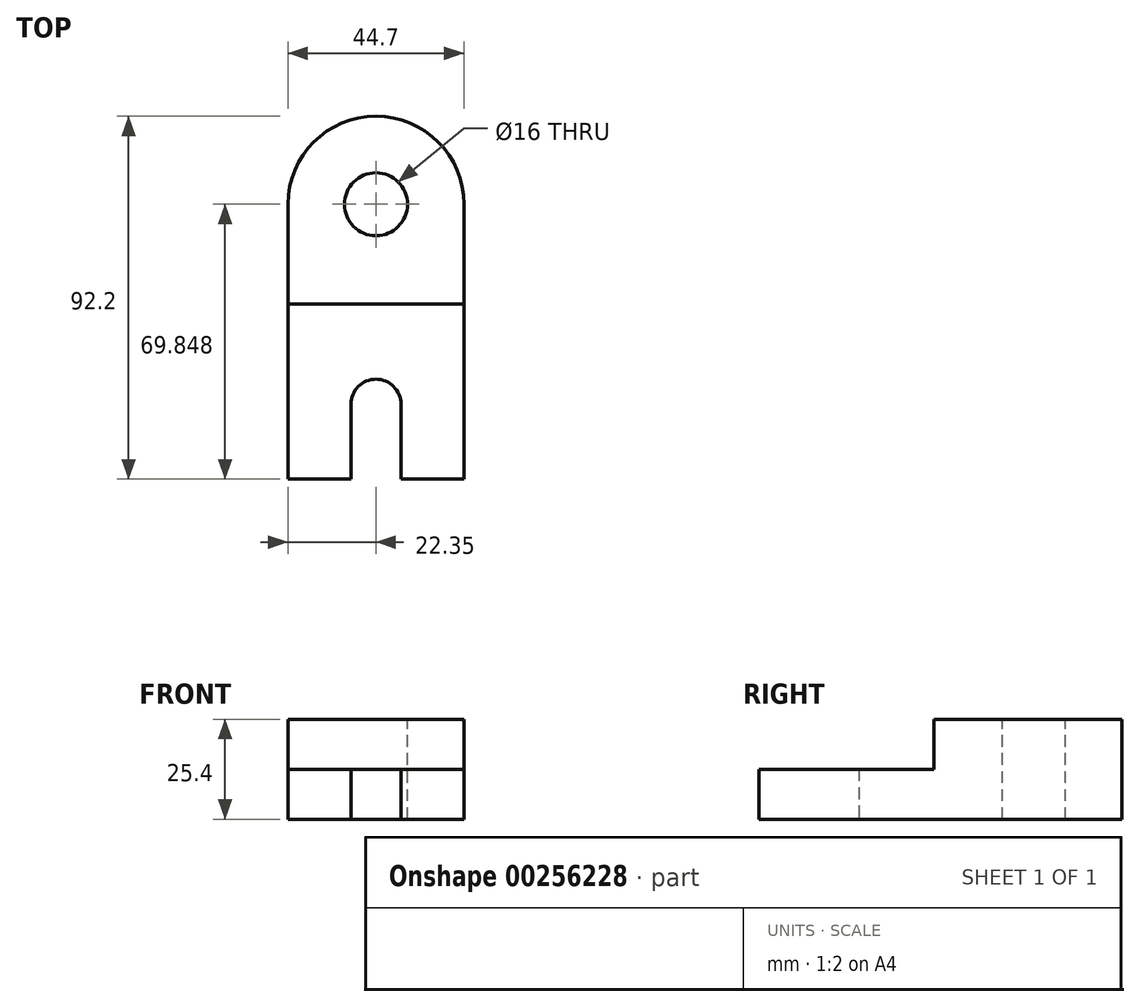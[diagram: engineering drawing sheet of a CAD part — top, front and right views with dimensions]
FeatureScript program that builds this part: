
annotation { "Feature Type Name" : "Feature", "Feature Type Description" : "" }
export const myFeature = defineFeature(function(context is Context, id is Id, definition is map)
    precondition{}
    {
        {
            var Q0;
            Q0=qCreatedBy(makeId("Top.planeOp"),FACE);
            var sketch = newSketch(context, id + "F0", { "sketchPlane" : qUnion([Q0])});
            skLineSegment(sketch, "E0", {"start": v(-5.13, 29.77) * mm, "end": v(-5.13, -40.08) * mm});
            skLineSegment(sketch, "E1", {"start": v(-49.83, 29.77) * mm, "end": v(-49.83, -40.08) * mm});
            skArc(sketch, "E2", {"start": v(-5.13, 29.77) * mm, "mid": v(-27.48, 52.12) * mm, "end": v(-49.83, 29.77) * mm});
            skLineSegment(sketch, "E3", {"start": v(-49.83, -40.08) * mm, "end": v(-33.83, -40.08) * mm});
            skLineSegment(sketch, "E4", {"start": v(-5.13, -40.08) * mm, "end": v(-21.13, -40.08) * mm});
            skLineSegment(sketch, "E5", {"start": v(-21.13, -40.08) * mm, "end": v(-21.13, -21.03) * mm});
            skLineSegment(sketch, "E6", {"start": v(-33.83, -40.08) * mm, "end": v(-33.83, -21.03) * mm});
            skArc(sketch, "E7", {"start": v(-21.13, -21.03) * mm, "mid": v(-27.48, -14.68) * mm, "end": v(-33.83, -21.03) * mm});
            skSolve(sketch);
        }
        {
            var Q0;
            Q0=makeQuery(id+"F0.imprint","IMPRINT",FACE,{"disambiguationData":[TD([[makeQuery(id+"F0.imprint","IMPRINT",EDGE,{"derivedFrom":sQuery(id+"F0.wireOp",EDGE,"E0")}),-1.0]])]});
            extrude(context, id + "F1", {"entities" : qUnion([Q0]), "depth" : 12.7 * mm});
        }
        {
            var Q0;
            Q0=makeQuery(id+"F1.opExtrude","CAP_FACE",FACE,{"disambiguationData":[OSD([sQuery(id+"F0.wireOp",EDGE,"E0"),sQuery(id+"F0.wireOp",EDGE,"E1"),sQuery(id+"F0.wireOp",EDGE,"E2"),sQuery(id+"F0.wireOp",EDGE,"E3"),sQuery(id+"F0.wireOp",EDGE,"E4"),sQuery(id+"F0.wireOp",EDGE,"E5"),sQuery(id+"F0.wireOp",EDGE,"E6"),sQuery(id+"F0.wireOp",EDGE,"E7")])],"isStart":false});
            var sketch = newSketch(context, id + "F2", { "sketchPlane" : qUnion([Q0])});
            skLineSegment(sketch, "E8", {"start": v(-49.83, 4.37) * mm, "end": v(-5.13, 4.37) * mm});
            skLineSegment(sketch, "E9", {"start": v(-49.83, 4.37) * mm, "end": v(-49.83, 29.77) * mm});
            skLineSegment(sketch, "E10", {"start": v(-5.13, 4.37) * mm, "end": v(-5.13, 29.77) * mm});
            skArc(sketch, "E11", {"start": v(-5.13, 29.77) * mm, "mid": v(-27.48, 52.12) * mm, "end": v(-49.83, 29.77) * mm});
            skSolve(sketch);
        }
        {
            var Q0;
            Q0=makeQuery(id+"F2.imprint","IMPRINT",FACE,{"disambiguationData":[TD([[makeQuery(id+"F2.imprint","IMPRINT",EDGE,{"derivedFrom":sQuery(id+"F2.wireOp",EDGE,"E8")}),1.0]])]});
            extrude(context, id + "F3", {"entities" : qUnion([Q0]), "operationType" : NewBodyOperationType.ADD, "depth" : 12.7 * mm});
        }
        {
            var Q0;
            Q0=makeQuery(id+"F3.opExtrude","CAP_FACE",FACE,{"disambiguationData":[OSD([sQuery(id+"F2.wireOp",EDGE,"E8"),sQuery(id+"F2.wireOp",EDGE,"E9"),sQuery(id+"F2.wireOp",EDGE,"E10"),sQuery(id+"F2.wireOp",EDGE,"E11")])],"isStart":false});
            var sketch = newSketch(context, id + "F4", { "sketchPlane" : qUnion([Q0])});
            skCircle(sketch, "E12", {"center": v(-27.48, 29.77) * mm, "radius": 8 * mm});
            skSolve(sketch);
        }
        {
            var Q0;
            Q0=sQuery(id+"F4.wireOp",VERTEX,"E12.center");
            var Q1;
            Q1=makeQuery(id+"F1.opExtrude","SWEPT_BODY",BODY,{"disambiguationData":[OSD([sQuery(id+"F0.wireOp",EDGE,"E0"),sQuery(id+"F0.wireOp",EDGE,"E1"),sQuery(id+"F0.wireOp",EDGE,"E2"),sQuery(id+"F0.wireOp",EDGE,"E3"),sQuery(id+"F0.wireOp",EDGE,"E4"),sQuery(id+"F0.wireOp",EDGE,"E5"),sQuery(id+"F0.wireOp",EDGE,"E6"),sQuery(id+"F0.wireOp",EDGE,"E7")])]});
            hole(context, id + "F5", {"style" : HoleStyle.SIMPLE, "endStyle" : HoleEndStyle.THROUGH, "holeDiameter" : 16 * mm, "isTappedThrough" : true, "tappedDepth" : 12.7 * mm, "tapClearance" : 3, "locations" : qUnion([Q0]), "scope" : qUnion([Q1])});
        }
    });
